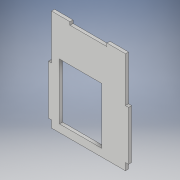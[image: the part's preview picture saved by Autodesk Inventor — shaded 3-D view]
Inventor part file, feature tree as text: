
AUTODESK INVENTOR PART (.ipt)
format: ipt  version: 2019 (Build 230136000, 136)  size: 135,168 bytes
history: native  units: in
note: dims shown in document units (in); Inventor stores cm internally (conversion verified against a paired STEP export)
features: extrude x4, sketch x4
ambient origin geometry x8: Origin, YZ Plane, XZ Plane, XY Plane, X Axis, Y Axis, Z Axis, Center Point
bodies: Solid1 (feature_tree)
feature tree (8):
  extrude  "Extrusion1"  Depth=3.111in
  extrude  "Extrusion2"  Depth=2.0in
  extrude  "Extrusion3"  Depth=0.125in
  extrude  "Extrusion4"  Depth=0.125in TaperAngle=0.0deg
  sketch  "Sketch1"  dims[d0=3.0in d1=3.111in]
  sketch  "Sketch2"  dims[d2=0.289in d3=2.0in]
  sketch  "Sketch3"  dims[d4=0.125in d5=0.0in d6=0.125in]
  sketch  "Sketch5"  dims[d7=1.0in d8=0.125in d9=0.0in d10=0.125in d11=1.5in d12=0.75in d13=0.125in d14=0.0in d15=1.0in d16=0.0in]
